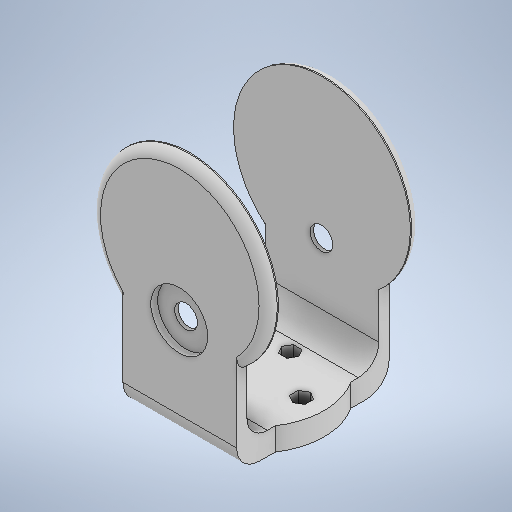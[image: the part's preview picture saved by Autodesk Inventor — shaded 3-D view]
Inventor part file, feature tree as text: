
AUTODESK INVENTOR PART (.ipt)
format: ipt  version: 2025.2 (Build 292293000, 293)  size: 372,736 bytes
history: native  units: mm
features: extrude x8, sketch x8, fillet x5, projected_geometry x3, plane x1
ambient origin geometry x8: Origin, YZ Plane, XZ Plane, XY Plane, X Axis, Y Axis, Z Axis, Center Point
bodies: Solid1 (feature_tree)
feature tree (25):
  extrude  "Extrusion1"  Depth=4.5mm
  sketch  "Sketch2"  dims[d5=50.0mm d9=58.0mm]
  fillet  "Fillet1"  Radius=60.0mm
  extrude  "Extrusion2"  Depth=58.0mm
  extrude  "Extrusion3"  Depth=10.0mm
  fillet  "Fillet2"  Radius=9.0mm
  plane  "Work Plane1"
  fillet  "Fillet3"  Radius=10.0mm
  extrude  "Extrusion4"  Depth=10.0mm
  fillet  "Fillet4"  Radius=10.0mm
  fillet  "Fillet5"  Radius=4.5mm
  extrude  "Extrusion5"  Depth=10.0mm
  extrude  "Extrusion6"  Depth=10.0mm
  extrude  "Extrusion7"  Depth=25.0mm
  extrude  "Extrusion9"  Depth=20.0mm TaperAngle=0.0deg
  sketch  "Sketch1"  dims[d0=4.5mm d1=4.5mm d4=60.0mm]
  projected_geometry  "Projected Loop1"
  sketch  "Sketch4"  dims[d10=50.0mm d11=0.0mm d12=60.0mm d13=9.0mm d14=10.0mm d15=0.0mm]
  sketch  "Sketch6"  dims[d16=4.5mm d17=0.0mm d18=4.0mm d19=10.0mm d20=4.5mm d21=0.0mm]
  projected_geometry  "Projected Loop3"
  sketch  "Sketch7"  dims[d22=10.0mm d23=4.0mm]
  sketch  "Sketch8"  dims[d24=36.0mm d25=10.0mm]
  sketch  "Sketch9"  dims[d26=0.0mm d27=0.0mm d28=25.0mm]
  sketch  "Sketch11"  dims[d29=3.0mm d30=0.0mm d31=3.0mm d32=0.0mm d43=15.0mm d44=20.0mm d45=0.0mm d46=0.0mm]
  projected_geometry  "Projected Loop6"
